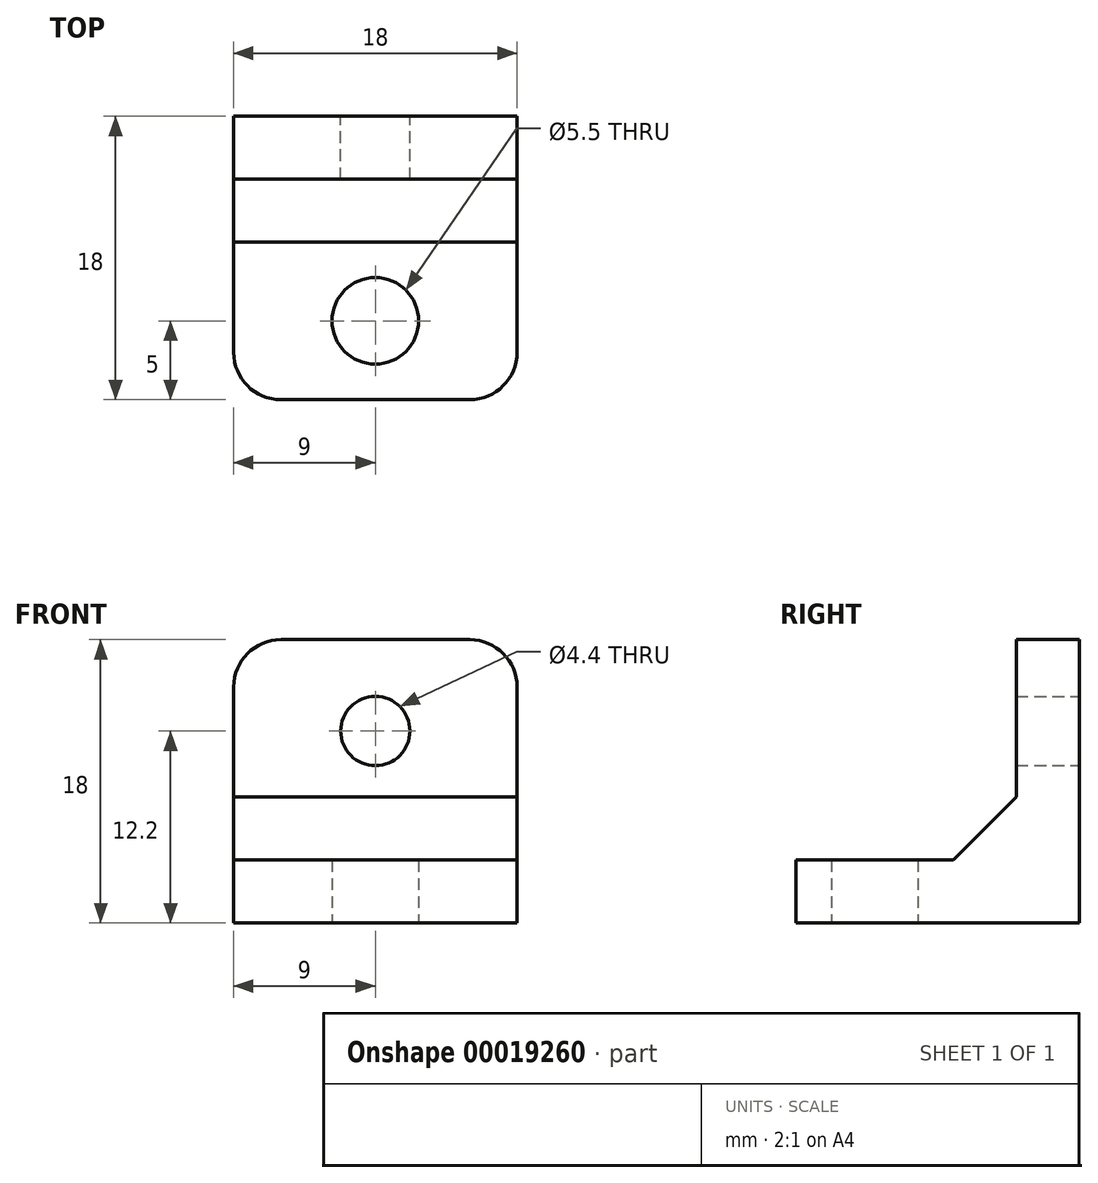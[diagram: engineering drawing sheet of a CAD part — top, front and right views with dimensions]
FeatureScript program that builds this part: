
annotation { "Feature Type Name" : "Feature", "Feature Type Description" : "" }
export const myFeature = defineFeature(function(context is Context, id is Id, definition is map)
    precondition{}
    {
        {
            var Q0;
            Q0=qCreatedBy(makeId("Front.planeOp"),FACE);
            var sketch = newSketch(context, id + "F0", { "sketchPlane" : qUnion([Q0])});
            skLineSegment(sketch, "E0.bottom", {"start": v(0, 0) * mm, "end": v(18, 0) * mm});
            skLineSegment(sketch, "E0.top", {"start": v(3, 18) * mm, "end": v(15, 18) * mm});
            skLineSegment(sketch, "E0.left", {"start": v(0, 0) * mm, "end": v(0, 15) * mm});
            skLineSegment(sketch, "E0.right", {"start": v(18, 0) * mm, "end": v(18, 15) * mm});
            skLineSegment(sketch, "E1", {"start": v(9, 18) * mm, "end": v(9, 0) * mm, "construction": true});
            skCircle(sketch, "E2", {"center": v(9, 12.2) * mm, "radius": 2.2 * mm});
            skPoint(sketch, "E3.visualSharp", {"position": v(0, 18) * mm});
            skArc(sketch, "E3.filletArc", {"start": v(3, 18) * mm, "mid": v(0.88, 17.12) * mm, "end": v(0, 15) * mm});
            skPoint(sketch, "E4.visualSharp", {"position": v(18, 18) * mm});
            skArc(sketch, "E4.filletArc", {"start": v(18, 15) * mm, "mid": v(17.12, 17.12) * mm, "end": v(15, 18) * mm});
            skSolve(sketch);
        }
        {
            var Q0;
            Q0=qCreatedBy(makeId("Top.planeOp"),FACE);
            var sketch = newSketch(context, id + "F1", { "sketchPlane" : qUnion([Q0])});
            skLineSegment(sketch, "E5.bottom", {"start": v(0, 0) * mm, "end": v(18, 0) * mm});
            skLineSegment(sketch, "E5.top", {"start": v(3, -18) * mm, "end": v(15, -18) * mm});
            skLineSegment(sketch, "E5.left", {"start": v(0, 0) * mm, "end": v(0, -15) * mm});
            skLineSegment(sketch, "E5.right", {"start": v(18, 0) * mm, "end": v(18, -15) * mm});
            skCircle(sketch, "E6", {"center": v(9, -13) * mm, "radius": 2.75 * mm});
            skCircle(sketch, "E7", {"center": v(9, -13) * mm, "radius": 5 * mm});
            skPoint(sketch, "E8.visualSharp", {"position": v(0, -18) * mm});
            skArc(sketch, "E8.filletArc", {"start": v(0, -15) * mm, "mid": v(0.88, -17.12) * mm, "end": v(3, -18) * mm});
            skPoint(sketch, "E9.visualSharp", {"position": v(18, -18) * mm});
            skArc(sketch, "E9.filletArc", {"start": v(15, -18) * mm, "mid": v(17.12, -17.12) * mm, "end": v(18, -15) * mm});
            skLineSegment(sketch, "E10", {"start": v(9, 0) * mm, "end": v(9, -18) * mm, "construction": true});
            skSolve(sketch);
        }
        {
            var Q0;
            Q0=makeQuery(id+"F1.imprint","IMPRINT",FACE,{"disambiguationData":[TD([[makeQuery(id+"F1.imprint","IMPRINT",EDGE,{"derivedFrom":sQuery(id+"F1.wireOp",EDGE,"E5.bottom")}),-1.0]])]});
            var Q1;
            Q1=makeQuery(id+"F1.imprint","IMPRINT",FACE,{"disambiguationData":[TD([[makeQuery(id+"F1.imprint","IMPRINT",EDGE,{"derivedFrom":sQuery(id+"F1.wireOp",EDGE,"E6")}),-1.0]])]});
            extrude(context, id + "F2", {"entities" : qUnion([Q0, Q1]), "depth" : 4 * mm});
        }
        {
            var Q0;
            Q0=makeQuery(id+"F0.imprint","IMPRINT",FACE,{"disambiguationData":[TD([[makeQuery(id+"F0.imprint","IMPRINT",EDGE,{"derivedFrom":sQuery(id+"F0.wireOp",EDGE,"E0.bottom")}),1.0]])]});
            extrude(context, id + "F3", {"entities" : qUnion([Q0]), "operationType" : NewBodyOperationType.ADD, "depth" : 4 * mm});
        }
        {
            var Q0;
            Q0=makeQuery(id+"F3.boolean.opBoolean","INTERSECT",EDGE,{"derivedFrom":[makeQuery(id+"F2.opExtrude","CAP_FACE",FACE,{"disambiguationData":[OSD([sQuery(id+"F1.wireOp",EDGE,"E5.bottom"),sQuery(id+"F1.wireOp",EDGE,"E5.top"),sQuery(id+"F1.wireOp",EDGE,"E5.left"),sQuery(id+"F1.wireOp",EDGE,"E5.right"),sQuery(id+"F1.wireOp",EDGE,"E6"),sQuery(id+"F1.wireOp",EDGE,"E8.filletArc"),sQuery(id+"F1.wireOp",EDGE,"E9.filletArc")])],"isStart":false}),makeQuery(id+"F3.opExtrude","CAP_FACE",FACE,{"disambiguationData":[OSD([sQuery(id+"F0.wireOp",EDGE,"E0.bottom"),sQuery(id+"F0.wireOp",EDGE,"E0.top"),sQuery(id+"F0.wireOp",EDGE,"E0.left"),sQuery(id+"F0.wireOp",EDGE,"E0.right"),sQuery(id+"F0.wireOp",EDGE,"E2"),sQuery(id+"F0.wireOp",EDGE,"0a5440e6-1312-472b-866a-db08221573ad"),sQuery(id+"F0.wireOp",EDGE,"E3.filletArc"),sQuery(id+"F0.wireOp",EDGE,"E4.filletArc")])],"isStart":false})]});
            chamfer(context, id + "F4", {"entities" : qUnion([Q0]), "width" : 4 * mm, "tangentPropagation" : true});
        }
    });
